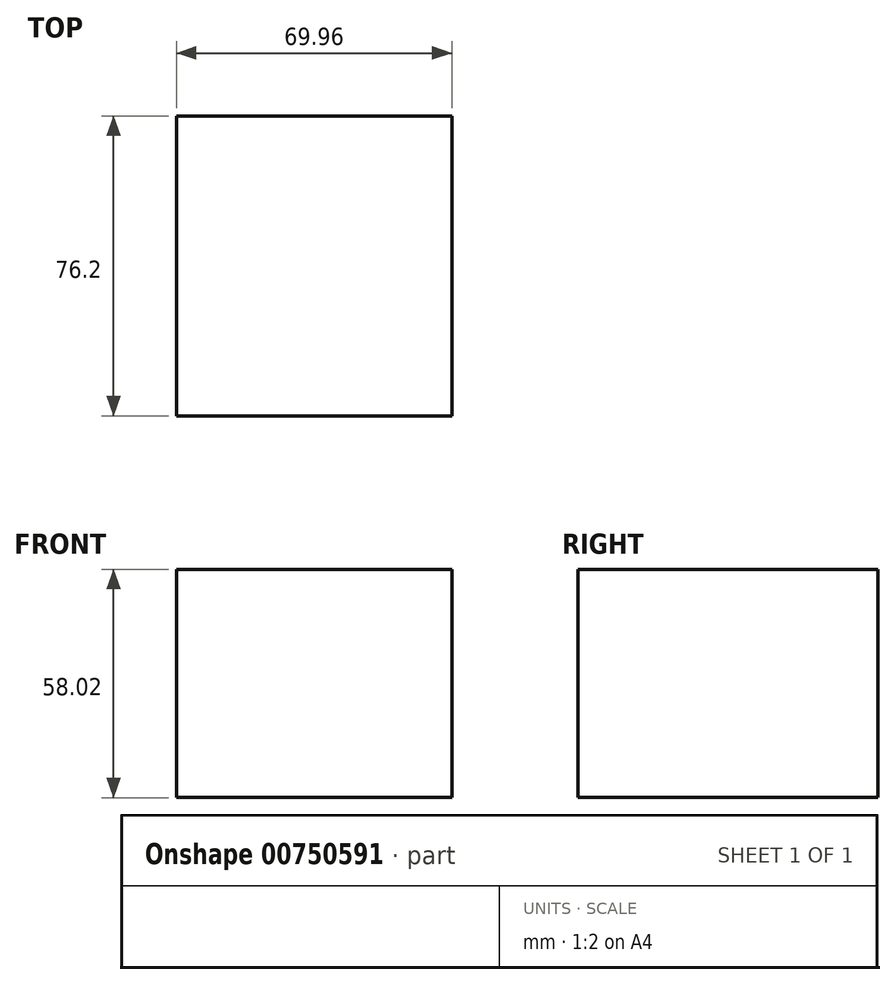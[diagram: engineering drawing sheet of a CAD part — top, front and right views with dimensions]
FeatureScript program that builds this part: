
annotation { "Feature Type Name" : "Feature", "Feature Type Description" : "" }
export const myFeature = defineFeature(function(context is Context, id is Id, definition is map)
    precondition{}
    {
        {
            var Q0;
            Q0=qCreatedBy(makeId("Front.planeOp"),FACE);
            var sketch = newSketch(context, id + "F0", { "sketchPlane" : qUnion([Q0])});
            skLineSegment(sketch, "E0.bottom", {"start": v(-34.03, -23.04) * mm, "end": v(35.93, -23.04) * mm});
            skLineSegment(sketch, "E0.top", {"start": v(-34.03, 34.98) * mm, "end": v(35.93, 34.98) * mm});
            skLineSegment(sketch, "E0.left", {"start": v(-34.03, -23.04) * mm, "end": v(-34.03, 34.98) * mm});
            skLineSegment(sketch, "E0.right", {"start": v(35.93, -23.04) * mm, "end": v(35.93, 34.98) * mm});
            skSolve(sketch);
        }
        {
            var Q0;
            Q0=makeQuery(id+"F0.imprint","IMPRINT",FACE,{"disambiguationData":[TD([[makeQuery(id+"F0.imprint","IMPRINT",EDGE,{"derivedFrom":sQuery(id+"F0.wireOp",EDGE,"E0.bottom")}),1.0]])]});
            extrude(context, id + "F1", {"entities" : qUnion([Q0]), "oppositeDirection" : true, "depth" : 76.2 * mm, "offsetDistance" : 25.4 * mm});
        }
    });
